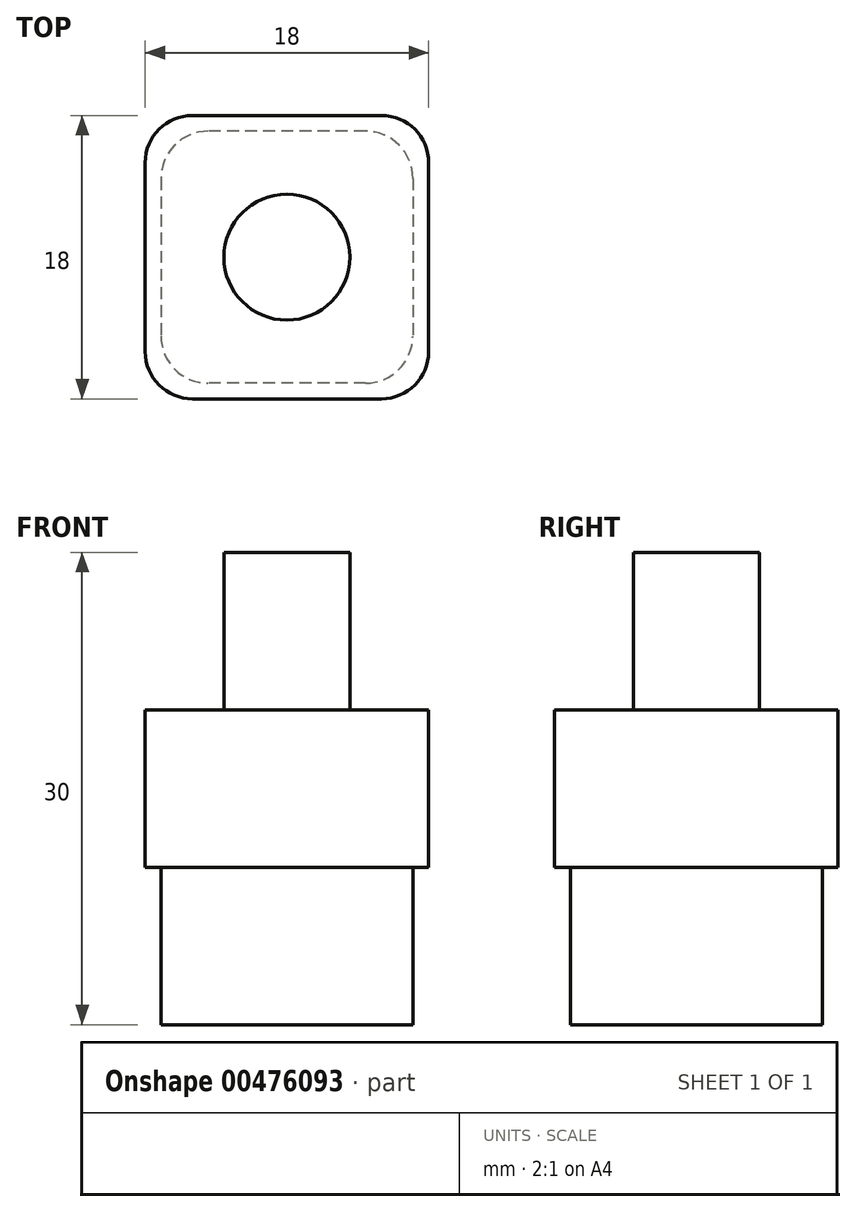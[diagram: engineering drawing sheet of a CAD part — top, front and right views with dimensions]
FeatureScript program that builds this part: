
annotation { "Feature Type Name" : "Feature", "Feature Type Description" : "" }
export const myFeature = defineFeature(function(context is Context, id is Id, definition is map)
    precondition{}
    {
        {
            var Q0;
            Q0=qCreatedBy(makeId("Top.planeOp"),FACE);
            var sketch = newSketch(context, id + "F0", { "sketchPlane" : qUnion([Q0])});
            skLineSegment(sketch, "E0.bottom", {"start": v(-3, 0) * mm, "end": v(-13, 0) * mm});
            skLineSegment(sketch, "E0.top", {"start": v(-3, -16) * mm, "end": v(-13, -16) * mm});
            skLineSegment(sketch, "E0.left", {"start": v(0, -3) * mm, "end": v(0, -13) * mm});
            skLineSegment(sketch, "E0.right", {"start": v(-16, -3) * mm, "end": v(-16, -13) * mm});
            skPoint(sketch, "E1.visualSharp", {"position": v(-16, -16) * mm});
            skArc(sketch, "E1.filletArc", {"start": v(-16, -13) * mm, "mid": v(-15.12, -15.12) * mm, "end": v(-13, -16) * mm});
            skPoint(sketch, "E2.visualSharp", {"position": v(0, -16) * mm});
            skArc(sketch, "E2.filletArc", {"start": v(-3, -16) * mm, "mid": v(-0.88, -15.12) * mm, "end": v(0, -13) * mm});
            skPoint(sketch, "E3.visualSharp", {"position": v(0, 0) * mm});
            skArc(sketch, "E3.filletArc", {"start": v(0, -3) * mm, "mid": v(-0.88, -0.88) * mm, "end": v(-3, 0) * mm});
            skPoint(sketch, "E4.visualSharp", {"position": v(-16, 0) * mm});
            skArc(sketch, "E4.filletArc", {"start": v(-13, 0) * mm, "mid": v(-15.12, -0.88) * mm, "end": v(-16, -3) * mm});
            skSolve(sketch);
        }
        {
            var Q0;
            Q0=makeQuery(id+"F0.imprint","IMPRINT",FACE,{"disambiguationData":[TD([[makeQuery(id+"F0.imprint","IMPRINT",EDGE,{"derivedFrom":sQuery(id+"F0.wireOp",EDGE,"E0.bottom")}),1.0]])]});
            extrude(context, id + "F1", {"entities" : qUnion([Q0]), "depth" : 10 * mm});
        }
        {
            var Q0;
            Q0=makeQuery(id+"F1.opExtrude","CAP_FACE",FACE,{"disambiguationData":[OSD([sQuery(id+"F0.wireOp",EDGE,"E0.bottom"),sQuery(id+"F0.wireOp",EDGE,"E0.top"),sQuery(id+"F0.wireOp",EDGE,"E0.left"),sQuery(id+"F0.wireOp",EDGE,"E0.right"),sQuery(id+"F0.wireOp",EDGE,"E1.filletArc"),sQuery(id+"F0.wireOp",EDGE,"E2.filletArc"),sQuery(id+"F0.wireOp",EDGE,"E3.filletArc"),sQuery(id+"F0.wireOp",EDGE,"E4.filletArc")])],"isStart":false});
            var sketch = newSketch(context, id + "F2", { "sketchPlane" : qUnion([Q0])});
            skLineSegment(sketch, "E5.bottom", {"start": v(-14, 1) * mm, "end": v(-2, 1) * mm});
            skLineSegment(sketch, "E5.top", {"start": v(-14, -17) * mm, "end": v(-2, -17) * mm});
            skLineSegment(sketch, "E5.left", {"start": v(-17, -2) * mm, "end": v(-17, -14) * mm});
            skLineSegment(sketch, "E5.right", {"start": v(1, -2) * mm, "end": v(1, -14) * mm});
            skPoint(sketch, "E5.middle", {"position": v(-8, -8) * mm});
            skPoint(sketch, "E5.middle.positionSnap0", {"position": v(0, -8) * mm});
            skPoint(sketch, "E5.middle.positionSnap1", {"position": v(-8, 0) * mm});
            skPoint(sketch, "E5.centerSnap0", {"position": v(0, -8) * mm});
            skPoint(sketch, "E5.centerSnap1", {"position": v(-8, 0) * mm});
            skPoint(sketch, "E6.visualSharp", {"position": v(-17, -17) * mm});
            skArc(sketch, "E6.filletArc", {"start": v(-17, -14) * mm, "mid": v(-16.12, -16.12) * mm, "end": v(-14, -17) * mm});
            skPoint(sketch, "E7.visualSharp", {"position": v(1, -17) * mm});
            skArc(sketch, "E7.filletArc", {"start": v(-2, -17) * mm, "mid": v(0.12, -16.12) * mm, "end": v(1, -14) * mm});
            skPoint(sketch, "E8.visualSharp", {"position": v(1, 1) * mm});
            skArc(sketch, "E8.filletArc", {"start": v(1, -2) * mm, "mid": v(0.12, 0.12) * mm, "end": v(-2, 1) * mm});
            skPoint(sketch, "E9.visualSharp", {"position": v(-17, 1) * mm});
            skArc(sketch, "E9.filletArc", {"start": v(-14, 1) * mm, "mid": v(-16.12, 0.12) * mm, "end": v(-17, -2) * mm});
            skSolve(sketch);
        }
        {
            var Q0;
            Q0 = qSketchRegion(id + "F2", true);
            extrude(context, id + "F3", {"entities" : qUnion([Q0]), "operationType" : NewBodyOperationType.ADD, "depth" : 10 * mm});
        }
        {
            var Q0;
            Q0=makeQuery(id+"F3.opExtrude","CAP_FACE",FACE,{"disambiguationData":[OSD([sQuery(id+"F2.wireOp",EDGE,"E5.bottom"),sQuery(id+"F2.wireOp",EDGE,"E5.top"),sQuery(id+"F2.wireOp",EDGE,"E5.left"),sQuery(id+"F2.wireOp",EDGE,"E5.right"),sQuery(id+"F2.wireOp",EDGE,"E6.filletArc"),sQuery(id+"F2.wireOp",EDGE,"E7.filletArc"),sQuery(id+"F2.wireOp",EDGE,"E8.filletArc"),sQuery(id+"F2.wireOp",EDGE,"E9.filletArc")])],"isStart":false});
            var sketch = newSketch(context, id + "F4", { "sketchPlane" : qUnion([Q0])});
            skCircle(sketch, "E10", {"center": v(-8, -8) * mm, "radius": 4 * mm});
            skPoint(sketch, "E10.centerSnap0", {"position": v(1, -8) * mm});
            skPoint(sketch, "E10.centerSnap1", {"position": v(-8, 1) * mm});
            skSolve(sketch);
        }
        {
            var Q0;
            Q0=makeQuery(id+"F4.imprint","IMPRINT",FACE,{"disambiguationData":[TD([[makeQuery(id+"F4.imprint","IMPRINT",EDGE,{"derivedFrom":sQuery(id+"F4.wireOp",EDGE,"E10")}),1.0]])]});
            extrude(context, id + "F5", {"entities" : qUnion([Q0]), "operationType" : NewBodyOperationType.ADD, "depth" : 10 * mm});
        }
    });
